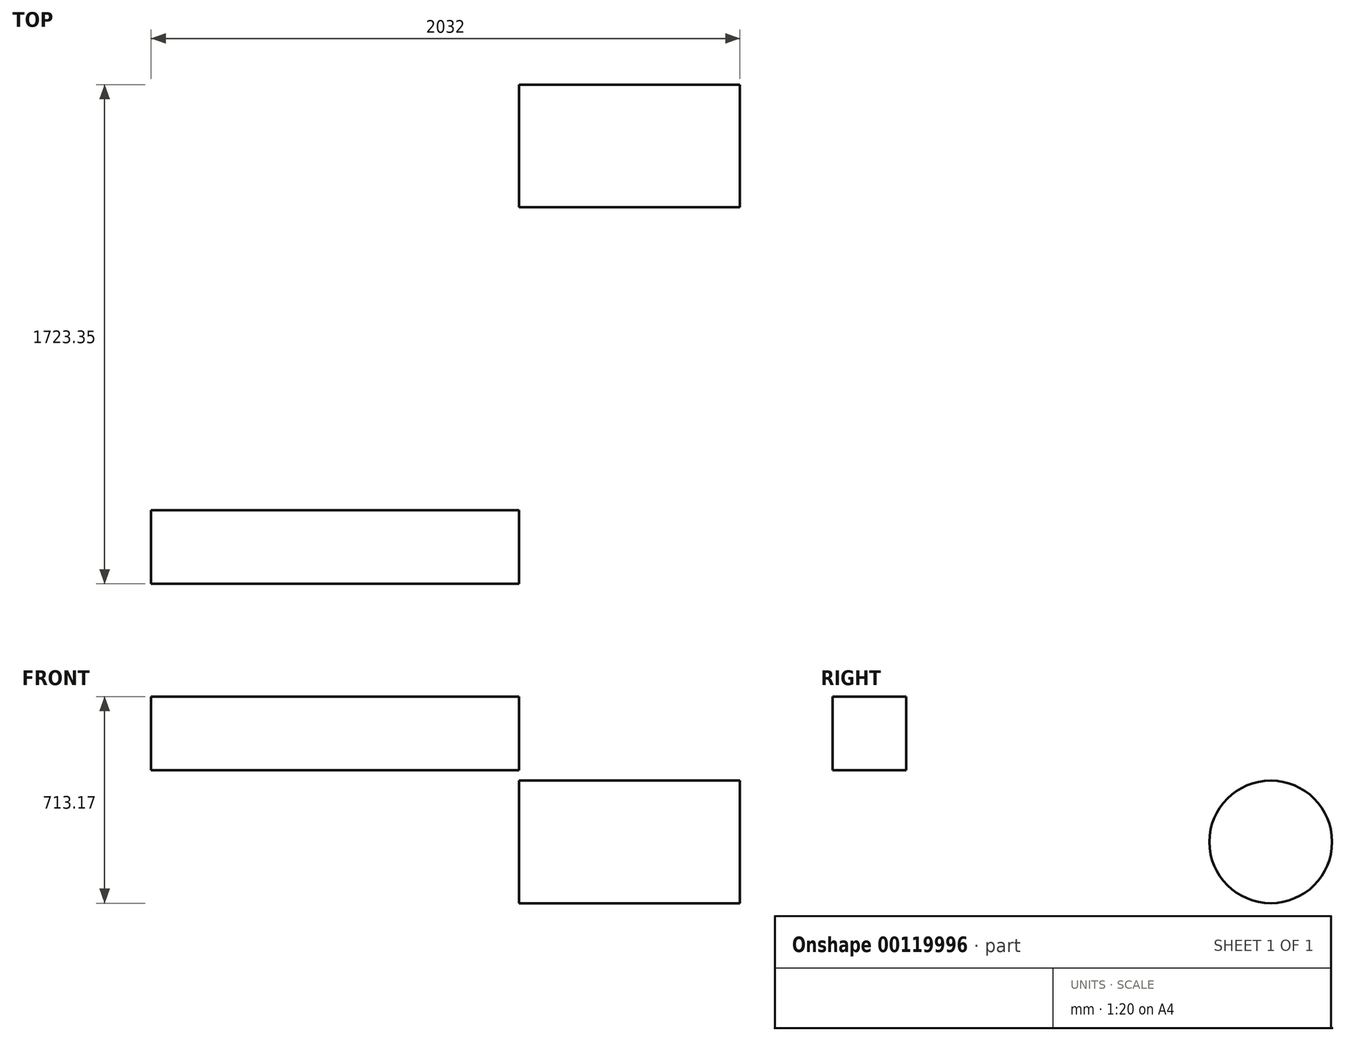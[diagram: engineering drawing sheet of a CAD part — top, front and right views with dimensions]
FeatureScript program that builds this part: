
annotation { "Feature Type Name" : "Feature", "Feature Type Description" : "" }
export const myFeature = defineFeature(function(context is Context, id is Id, definition is map)
    precondition{}
    {
        {
            var Q0;
            Q0=qCreatedBy(makeId("Front.planeOp"),FACE);
            var sketch = newSketch(context, id + "F0", { "sketchPlane" : qUnion([Q0])});
            skLineSegment(sketch, "E0.bottom", {"start": v(-1270, 9.4) * mm, "end": v(0, 9.4) * mm});
            skLineSegment(sketch, "E0.top", {"start": v(-1270, -244.6) * mm, "end": v(0, -244.6) * mm});
            skLineSegment(sketch, "E0.left", {"start": v(-1270, 9.4) * mm, "end": v(-1270, -244.6) * mm});
            skLineSegment(sketch, "E0.right", {"start": v(0, 9.4) * mm, "end": v(0, -244.6) * mm});
            skSolve(sketch);
        }
        {
            var Q0;
            Q0 = qSketchRegion(id + "F0", true);
            extrude(context, id + "F1", {"entities" : qUnion([Q0]), "depth" : 254 * mm});
        }
        {
            var Q0;
            Q0=qCreatedBy(makeId("Right.planeOp"),FACE);
            var sketch = newSketch(context, id + "F2", { "sketchPlane" : qUnion([Q0])});
            skCircle(sketch, "E1", {"center": v(1257.77, -492.2) * mm, "radius": 211.58 * mm});
            skSolve(sketch);
        }
        {
            var Q0;
            Q0 = qSketchRegion(id + "F2", true);
            extrude(context, id + "F3", {"entities" : qUnion([Q0]), "depth" : 762 * mm});
        }
    });
